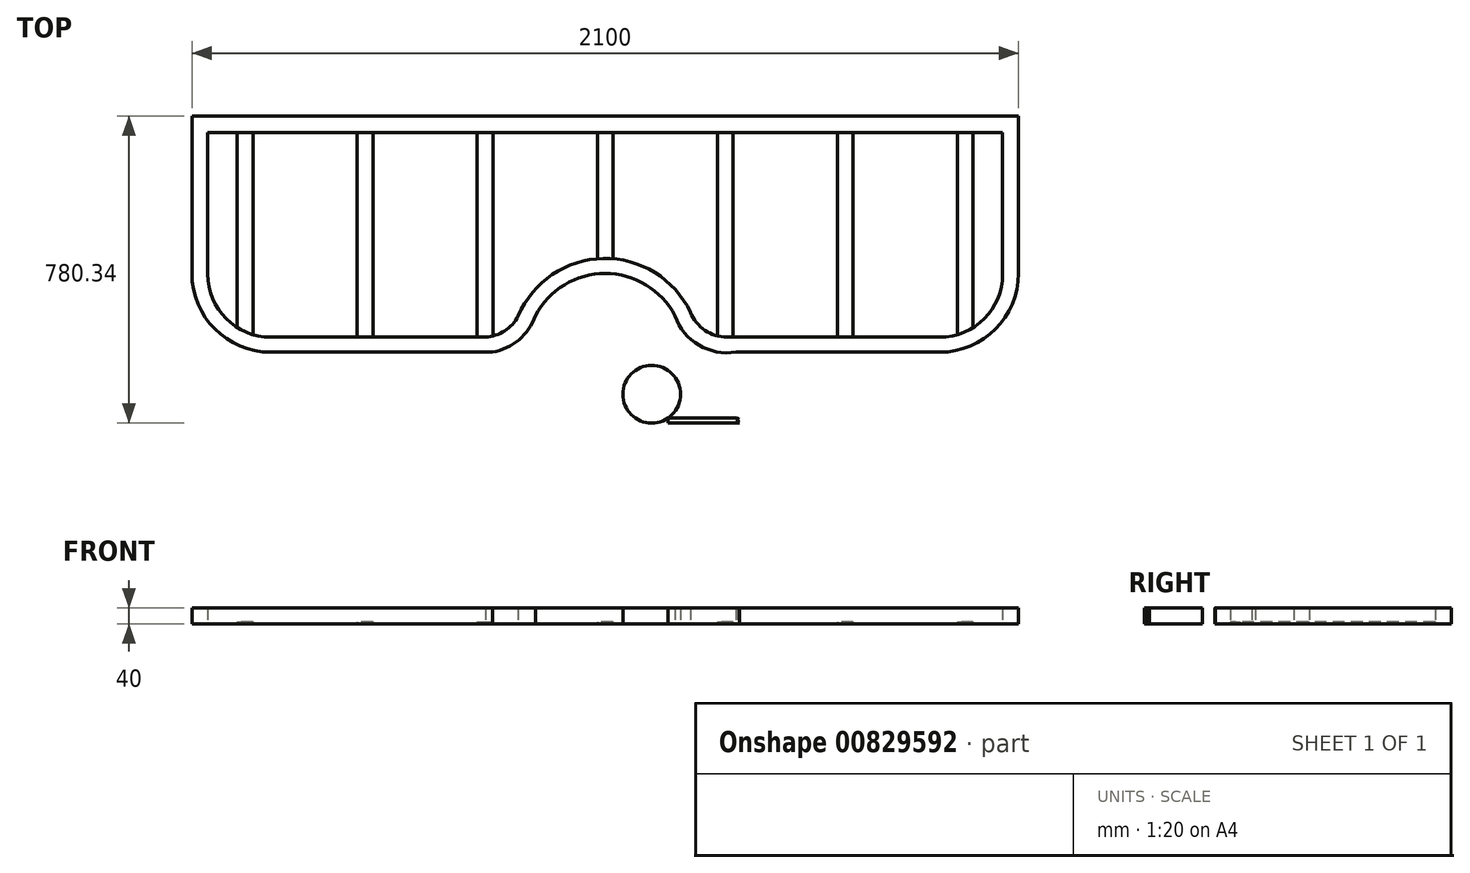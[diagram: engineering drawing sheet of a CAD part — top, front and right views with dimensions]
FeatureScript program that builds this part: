
annotation { "Feature Type Name" : "Feature", "Feature Type Description" : "" }
export const myFeature = defineFeature(function(context is Context, id is Id, definition is map)
    precondition{}
    {
        {
            var Q0;
            Q0=qCreatedBy(makeId("Top.planeOp"),FACE);
            var sketch = newSketch(context, id + "F0", { "sketchPlane" : qUnion([Q0])});
            skLineSegment(sketch, "E0.bottom", {"start": v(-1066.2, 294.61) * mm, "end": v(1033.8, 294.61) * mm});
            skLineSegment(sketch, "E0.top", {"start": v(-866.2, -305.39) * mm, "end": v(-302.67, -305.39) * mm});
            skLineSegment(sketch, "E0.left", {"start": v(-1066.2, 294.61) * mm, "end": v(-1066.2, -105.39) * mm});
            skLineSegment(sketch, "E0.right", {"start": v(1033.8, 294.61) * mm, "end": v(1033.8, -105.39) * mm});
            skLineSegment(sketch, "E1", {"start": v(-1026.2, 252.8) * mm, "end": v(-1026.2, -107.2) * mm});
            skLineSegment(sketch, "E2", {"start": v(-866.2, -267.2) * mm, "end": v(-320.67, -267.2) * mm});
            skLineSegment(sketch, "E3", {"start": v(993.8, -107.2) * mm, "end": v(993.8, 252.8) * mm});
            skLineSegment(sketch, "E4", {"start": v(993.8, 252.8) * mm, "end": v(-301.2, 252.8) * mm});
            skArc(sketch, "E5.filletArc", {"start": v(-1026.2, -107.2) * mm, "mid": v(-979.35, -220.33) * mm, "end": v(-866.2, -267.2) * mm});
            skArc(sketch, "E6.filletArc", {"start": v(833.8, -267.2) * mm, "mid": v(946.93, -220.33) * mm, "end": v(993.8, -107.2) * mm});
            skPoint(sketch, "E7.visualSharp", {"position": v(-1066.2, -305.39) * mm});
            skArc(sketch, "E7.filletArc", {"start": v(-1066.2, -105.39) * mm, "mid": v(-1007.63, -246.8) * mm, "end": v(-866.2, -305.39) * mm});
            skArc(sketch, "E8.filletArc", {"start": v(833.8, -305.39) * mm, "mid": v(975.21, -246.8) * mm, "end": v(1033.8, -105.39) * mm});
            skPoint(sketch, "E9", {"position": v(-16.2, -305.39) * mm});
            skPoint(sketch, "E10", {"position": v(-16.2, -107.2) * mm});
            skArc(sketch, "E11", {"start": v(171, -235) * mm, "mid": v(-4.05, -105.76) * mm, "end": v(-193.49, -212.8) * mm});
            skArc(sketch, "E12", {"start": v(-320.67, -267.2) * mm, "mid": v(-271.66, -251.34) * mm, "end": v(-237.04, -213.2) * mm});
            skArc(sketch, "E13", {"start": v(-302.67, -305.39) * mm, "mid": v(-235.35, -274.1) * mm, "end": v(-193.49, -212.8) * mm});
            skArc(sketch, "E14", {"start": v(200.63, -204.32) * mm, "mid": v(237.41, -250) * mm, "end": v(293.48, -267.2) * mm});
            skArc(sketch, "E15", {"start": v(161.2, -213.06) * mm, "mid": v(221.72, -287.4) * mm, "end": v(315.88, -305.39) * mm});
            skLineSegment(sketch, "E16.trimOffspring", {"start": v(391.46, -267.2) * mm, "end": v(833.8, -267.2) * mm});
            skLineSegment(sketch, "E17.trimOffspring", {"start": v(315.88, -305.39) * mm, "end": v(833.8, -305.39) * mm});
            skArc(sketch, "E18.trimOffspring", {"start": v(204.26, -212.37) * mm, "mid": v(-16.66, -67.2) * mm, "end": v(-237.04, -213.2) * mm});
            skLineSegment(sketch, "E19", {"start": v(293.48, -267.2) * mm, "end": v(391.46, -267.2) * mm});
            skLineSegment(sketch, "E20", {"start": v(-951.2, 252.8) * mm, "end": v(-951.2, -242.74) * mm});
            skLineSegment(sketch, "E21", {"start": v(-911.2, 252.8) * mm, "end": v(-911.2, -260.73) * mm});
            skPoint(sketch, "E22", {"position": v(-16.2, 252.8) * mm});
            skLineSegment(sketch, "E23", {"start": v(-36.2, 252.8) * mm, "end": v(-36.2, -68.03) * mm});
            skLineSegment(sketch, "E24", {"start": v(3.8, 252.8) * mm, "end": v(3.8, -68.03) * mm});
            skLineSegment(sketch, "E25", {"start": v(-646.2, 252.8) * mm, "end": v(-646.2, -267.2) * mm});
            skLineSegment(sketch, "E26", {"start": v(-606.2, 252.8) * mm, "end": v(-606.2, -267.2) * mm});
            skLineSegment(sketch, "E27.MirrorCS", {"start": v(918.8, 252.8) * mm, "end": v(918.8, -242.74) * mm});
            skLineSegment(sketch, "E28.MirrorCS", {"start": v(878.8, 252.8) * mm, "end": v(878.8, -260.73) * mm});
            skLineSegment(sketch, "E29.MirrorCS", {"start": v(613.8, 252.8) * mm, "end": v(613.8, -267.2) * mm});
            skLineSegment(sketch, "E30.MirrorCS", {"start": v(573.8, 252.8) * mm, "end": v(573.8, -267.2) * mm});
            skLineSegment(sketch, "E31.MirrorCS", {"start": v(308.8, 252.8) * mm, "end": v(308.8, -266.15) * mm});
            skLineSegment(sketch, "E32.MirrorCS", {"start": v(268.8, 252.8) * mm, "end": v(268.8, -264.23) * mm});
            skPoint(sketch, "E33.orphan", {"position": v(-16.2, 353.46) * mm});
            skCircle(sketch, "E34", {"center": v(101.96, -412.38) * mm, "radius": 73.35 * mm});
            skLineSegment(sketch, "E35", {"start": v(143.15, -485.73) * mm, "end": v(325.46, -485.73) * mm});
            skLineSegment(sketch, "E36", {"start": v(325.46, -485.73) * mm, "end": v(317.9, -481.8) * mm});
            skLineSegment(sketch, "E37", {"start": v(317.9, -481.8) * mm, "end": v(324.41, -476.5) * mm});
            skLineSegment(sketch, "E38", {"start": v(324.41, -476.5) * mm, "end": v(317.68, -473.07) * mm});
            skLineSegment(sketch, "E39", {"start": v(317.68, -473.07) * mm, "end": v(143.15, -473.07) * mm});
            skLineSegment(sketch, "E40", {"start": v(143.15, -473.07) * mm, "end": v(143.15, -485.73) * mm});
            skLineSegment(sketch, "E41", {"start": v(-341.2, 252.8) * mm, "end": v(-301.2, 252.8) * mm});
            skLineSegment(sketch, "E42.trimOffspring", {"start": v(-341.2, 252.8) * mm, "end": v(-1026.2, 252.8) * mm});
            skLineSegment(sketch, "E43", {"start": v(-341.2, 252.8) * mm, "end": v(-341.2, -267.2) * mm});
            skLineSegment(sketch, "E44", {"start": v(-301.2, 252.8) * mm, "end": v(-301.2, -264.23) * mm});
            skLineSegment(sketch, "E45", {"start": v(308.8, -266.15) * mm, "end": v(308.8, 252.8) * mm});
            skLineSegment(sketch, "E46", {"start": v(613.8, -267.2) * mm, "end": v(613.8, 252.8) * mm});
            skLineSegment(sketch, "E47", {"start": v(268.8, 252.8) * mm, "end": v(308.8, 252.8) * mm});
            skLineSegment(sketch, "E48", {"start": v(308.8, -266.15) * mm, "end": v(308.8, -267.2) * mm});
            skSolve(sketch);
        }
        {
            var Q0;
            {var subQ21=sQuery(id+"F0.wireOp",EDGE,"E15");var subQ22=sQuery(id+"F0.wireOp",EDGE,"E11");var subQ23=makeQuery(id+"F0.imprint","INTERSECT",VERTEX,{"disambiguationData":[OD(0.0)],"derivedFrom":[subQ22,subQ21]});var subQ33=makeQuery(id+"F0.imprint","IMPRINT",EDGE,{"disambiguationData":[TD([[subQ23,-1.0]])],"derivedFrom":subQ22});var subQ67=sQuery(id+"F0.wireOp",EDGE,"E39");var subQ68=sQuery(id+"F0.wireOp",EDGE,"E40");var subQ69=sQuery(id+"F0.wireOp",EDGE,"E34");Q0=qUnion([makeQuery(id+"F0.imprint","IMPRINT",FACE,{"disambiguationData":[TD([[makeQuery(id+"F0.imprint","IMPRINT",EDGE,{"disambiguationData":[TD([[makeQuery(id+"F0.imprint","INTERSECT",VERTEX,{"derivedFrom":[subQ69,subQ67,subQ68]}),-1.0]])],"derivedFrom":subQ69}),1.0]])]}),makeQuery(id+"F0.imprint","IMPRINT",FACE,{"disambiguationData":[TD([[makeQuery(id+"F0.imprint","IMPRINT",EDGE,{"derivedFrom":sQuery(id+"F0.wireOp",EDGE,"E35")}),1.0]])]}),makeQuery(id+"F0.imprint","IMPRINT",FACE,{"disambiguationData":[TD([[subQ33,1.0]])]}),makeQuery(id+"F0.imprint","IMPRINT",FACE,{"disambiguationData":[TD([[makeQuery(id+"F0.imprint","IMPRINT",EDGE,{"derivedFrom":sQuery(id+"F0.wireOp",EDGE,"E0.bottom")}),-1.0]])]})]);}
            extrude(context, id + "F1", {"entities" : qUnion([Q0]), "depth" : 40 * mm, "offsetDistance" : 25 * mm});
        }
        {
            var Q0;
            {var subQ0=sQuery(id+"F0.wireOp",EDGE,"E20");Q0=makeQuery(id+"F0.imprint","IMPRINT",FACE,{"disambiguationData":[TD([[makeQuery(id+"F0.imprint","IMPRINT",EDGE,{"derivedFrom":subQ0}),1.0]])]});}
            extrude(context, id + "F2", {"entities" : qUnion([Q0]), "operationType" : NewBodyOperationType.ADD, "depth" : 5 * mm, "offsetDistance" : 25 * mm});
        }
        {
            var Q0;
            {var subQ2=sQuery(id+"F0.wireOp",EDGE,"E25");Q0=makeQuery(id+"F0.imprint","IMPRINT",FACE,{"disambiguationData":[TD([[makeQuery(id+"F0.imprint","IMPRINT",EDGE,{"derivedFrom":subQ2}),1.0]])]});}
            extrude(context, id + "F3", {"entities" : qUnion([Q0]), "operationType" : NewBodyOperationType.ADD, "depth" : 5 * mm, "offsetDistance" : 25 * mm});
        }
        {
            var Q0;
            Q0=makeQuery(id+"F0.imprint","IMPRINT",FACE,{"disambiguationData":[TD([[makeQuery(id+"F0.imprint","IMPRINT",EDGE,{"derivedFrom":sQuery(id+"F0.wireOp",EDGE,"E41")}),-1.0]])]});
            extrude(context, id + "F4", {"entities" : qUnion([Q0]), "operationType" : NewBodyOperationType.ADD, "depth" : 5 * mm, "offsetDistance" : 25 * mm});
        }
        {
            var Q0;
            {var subQ0=sQuery(id+"F0.wireOp",EDGE,"E23");Q0=makeQuery(id+"F0.imprint","IMPRINT",FACE,{"disambiguationData":[TD([[makeQuery(id+"F0.imprint","IMPRINT",EDGE,{"derivedFrom":subQ0}),1.0]])]});}
            extrude(context, id + "F5", {"entities" : qUnion([Q0]), "operationType" : NewBodyOperationType.ADD, "depth" : 5 * mm, "offsetDistance" : 25 * mm});
        }
        {
            var Q0;
            {var subQ0=sQuery(id+"F0.wireOp",EDGE,"E31.MirrorCS");Q0=makeQuery(id+"F0.imprint","IMPRINT",FACE,{"disambiguationData":[TD([[makeQuery(id+"F0.imprint","IMPRINT",EDGE,{"derivedFrom":subQ0}),-1.0]])]});}
            extrude(context, id + "F6", {"entities" : qUnion([Q0]), "operationType" : NewBodyOperationType.ADD, "depth" : 5 * mm, "offsetDistance" : 25 * mm});
        }
        {
            var Q0;
            {var subQ2=sQuery(id+"F0.wireOp",EDGE,"E29.MirrorCS");Q0=makeQuery(id+"F0.imprint","IMPRINT",FACE,{"disambiguationData":[TD([[makeQuery(id+"F0.imprint","IMPRINT",EDGE,{"derivedFrom":subQ2}),-1.0]])]});}
            extrude(context, id + "F7", {"entities" : qUnion([Q0]), "operationType" : NewBodyOperationType.ADD, "depth" : 5 * mm, "offsetDistance" : 25 * mm});
        }
        {
            var Q0;
            {var subQ0=sQuery(id+"F0.wireOp",EDGE,"E27.MirrorCS");Q0=makeQuery(id+"F0.imprint","IMPRINT",FACE,{"disambiguationData":[TD([[makeQuery(id+"F0.imprint","IMPRINT",EDGE,{"derivedFrom":subQ0}),-1.0]])]});}
            extrude(context, id + "F8", {"entities" : qUnion([Q0]), "operationType" : NewBodyOperationType.ADD, "depth" : 5 * mm, "offsetDistance" : 25 * mm});
        }
    });
